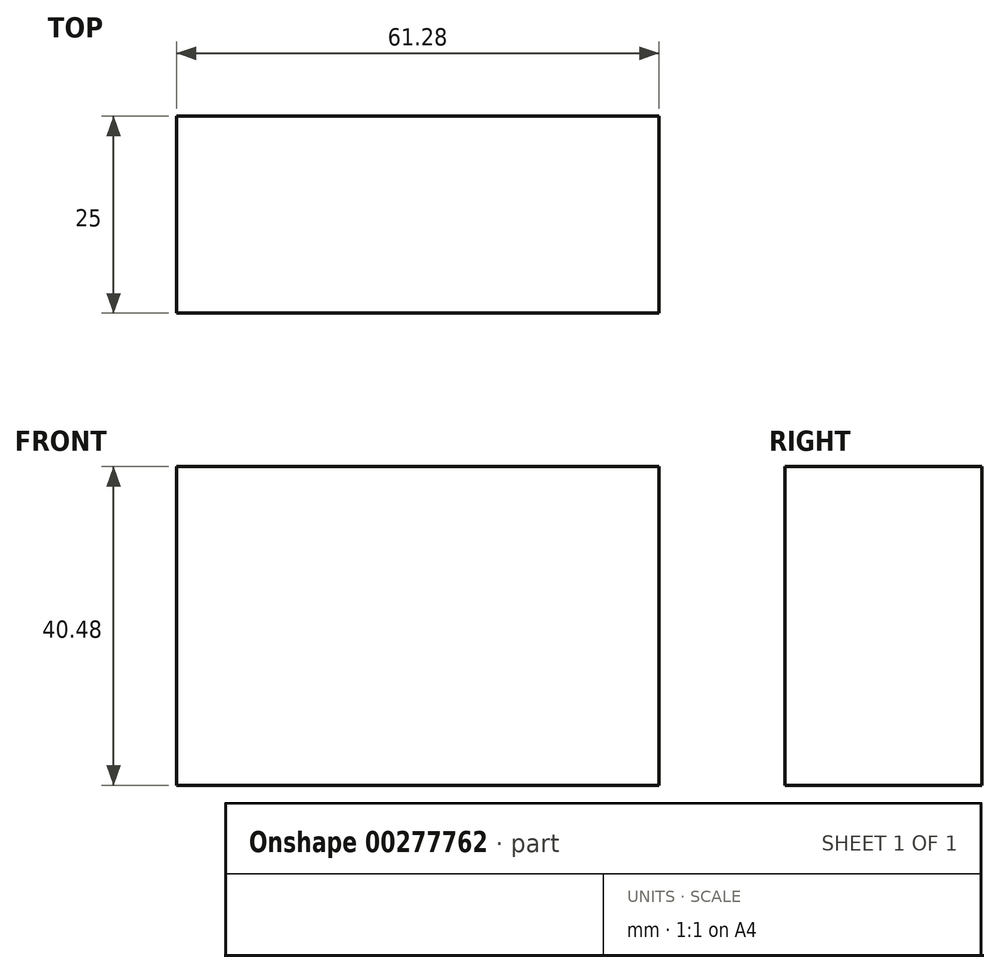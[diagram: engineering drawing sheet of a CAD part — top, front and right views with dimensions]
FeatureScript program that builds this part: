
annotation { "Feature Type Name" : "Feature", "Feature Type Description" : "" }
export const myFeature = defineFeature(function(context is Context, id is Id, definition is map)
    precondition{}
    {
        {
            var Q0;
            Q0=qCreatedBy(makeId("Front.planeOp"),FACE);
            var sketch = newSketch(context, id + "F0", { "sketchPlane" : qUnion([Q0])});
            skLineSegment(sketch, "E0.bottom", {"start": v(24.17, 26.42) * mm, "end": v(85.45, 26.42) * mm});
            skLineSegment(sketch, "E0.top", {"start": v(24.17, 66.9) * mm, "end": v(85.45, 66.9) * mm});
            skLineSegment(sketch, "E0.left", {"start": v(24.17, 26.42) * mm, "end": v(24.17, 66.9) * mm});
            skLineSegment(sketch, "E0.right", {"start": v(85.45, 26.42) * mm, "end": v(85.45, 66.9) * mm});
            skPoint(sketch, "E0.middle", {"position": v(54.8, 46.66) * mm});
            skSolve(sketch);
        }
        {
            var Q0;
            Q0=makeQuery(id+"F0.imprint","IMPRINT",FACE,{"disambiguationData":[TD([[makeQuery(id+"F0.imprint","IMPRINT",EDGE,{"derivedFrom":sQuery(id+"F0.wireOp",EDGE,"E0.bottom")}),1.0]])]});
            extrude(context, id + "F1", {"entities" : qUnion([Q0]), "depth" : 25 * mm});
        }
    });
